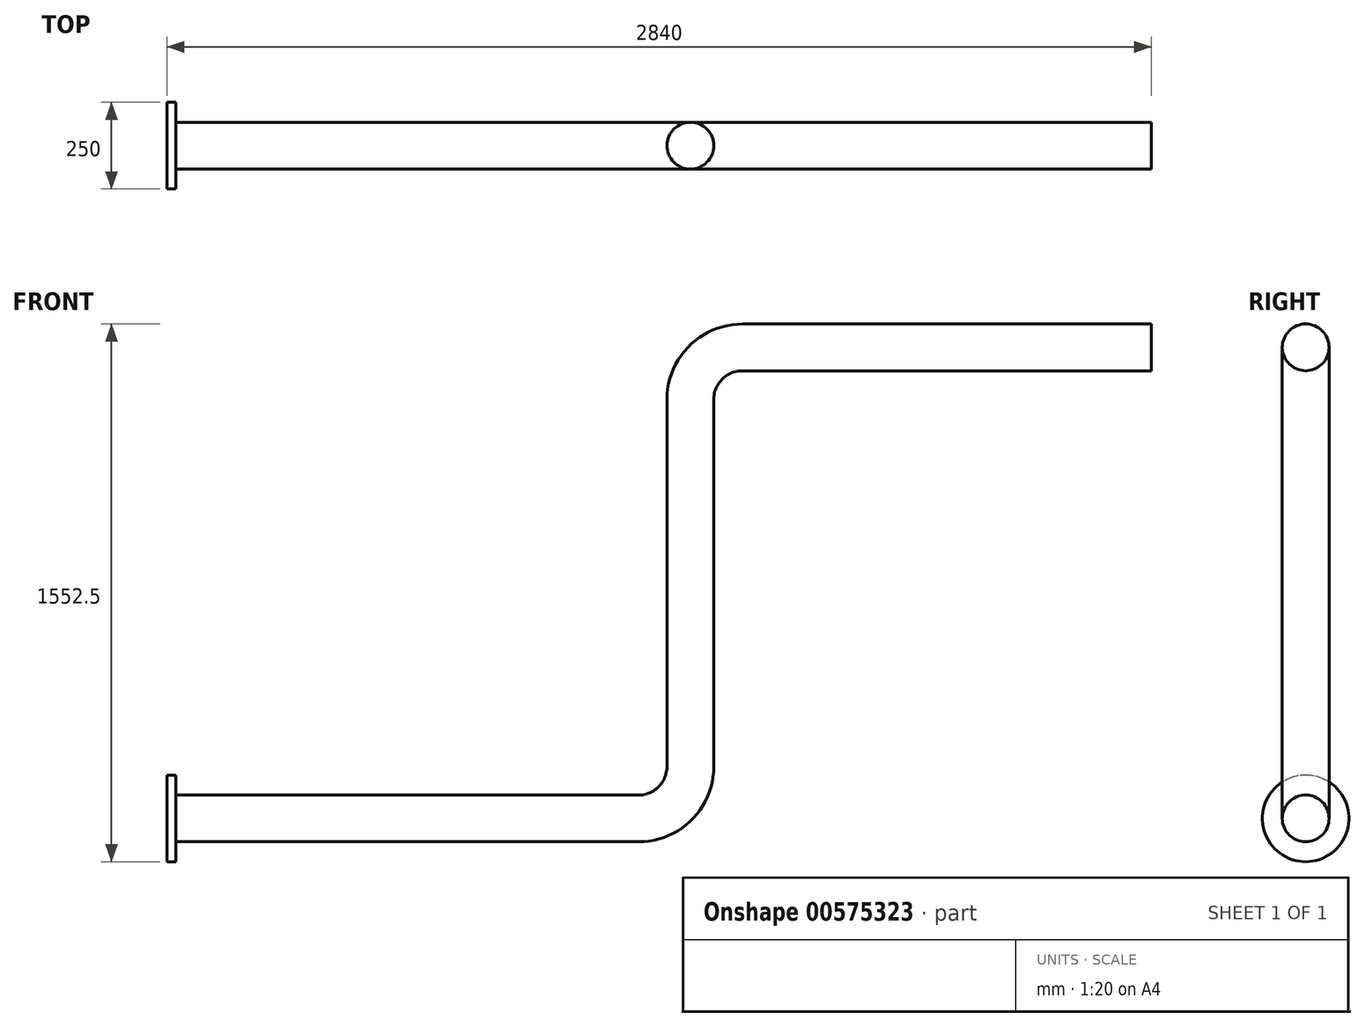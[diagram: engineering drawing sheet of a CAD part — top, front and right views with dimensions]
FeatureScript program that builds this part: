
annotation { "Feature Type Name" : "Feature", "Feature Type Description" : "" }
export const myFeature = defineFeature(function(context is Context, id is Id, definition is map)
    precondition{}
    {
        {
            var Q0;
            Q0=qCreatedBy(makeId("Right.planeOp"),FACE);
            var sketch = newSketch(context, id + "F0", { "sketchPlane" : qUnion([Q0])});
            skCircle(sketch, "E0", {"center": v(0, 0) * mm, "radius": 67.5 * mm});
            skCircle(sketch, "E1", {"center": v(0, 0) * mm, "radius": 125 * mm});
            skSolve(sketch);
        }
        {
            var Q0;
            Q0=qCreatedBy(makeId("Front.planeOp"),FACE);
            var sketch = newSketch(context, id + "F1", { "sketchPlane" : qUnion([Q0])});
            skLineSegment(sketch, "E2", {"start": v(0, 0) * mm, "end": v(1360, 0) * mm});
            skLineSegment(sketch, "E3", {"start": v(1510, 150) * mm, "end": v(1510, 1210) * mm});
            skLineSegment(sketch, "E4", {"start": v(1660, 1360) * mm, "end": v(2840, 1360) * mm});
            skPoint(sketch, "E5.visualSharp", {"position": v(1510, 1360) * mm});
            skArc(sketch, "E5.filletArc", {"start": v(1660, 1360) * mm, "mid": v(1553.93, 1316.07) * mm, "end": v(1510, 1210) * mm});
            skPoint(sketch, "E6.visualSharp", {"position": v(1510, 0) * mm});
            skArc(sketch, "E6.filletArc", {"start": v(1360, 0) * mm, "mid": v(1466.07, 43.93) * mm, "end": v(1510, 150) * mm});
            skSolve(sketch);
        }
        {
            var Q0;
            Q0=makeQuery(id+"F0.imprint","IMPRINT",FACE,{"disambiguationData":[TD([[makeQuery(id+"F0.imprint","IMPRINT",EDGE,{"derivedFrom":sQuery(id+"F0.wireOp",EDGE,"E0")}),1.0]])]});
            var Q1;
            Q1=sQuery(id+"F1.wireOp",EDGE,"E2");
            var Q2;
            Q2=sQuery(id+"F1.wireOp",EDGE,"E6.filletArc");
            var Q3;
            Q3=sQuery(id+"F1.wireOp",EDGE,"E3");
            var Q4;
            Q4=sQuery(id+"F1.wireOp",EDGE,"E5.filletArc");
            var Q5;
            Q5=sQuery(id+"F1.wireOp",EDGE,"E4");
            sweep(context, id + "F2", {"profiles" : qUnion([Q0]), "path" : qUnion([Q1, Q2, Q3, Q4, Q5])});
        }
        {
            var Q0;
            Q0=makeQuery(id+"F0.imprint","IMPRINT",FACE,{"disambiguationData":[TD([[makeQuery(id+"F0.imprint","IMPRINT",EDGE,{"derivedFrom":sQuery(id+"F0.wireOp",EDGE,"E0")}),-1.0]])]});
            extrude(context, id + "F3", {"entities" : qUnion([Q0]), "operationType" : NewBodyOperationType.ADD, "depth" : 25 * mm, "offsetDistance" : 25 * mm});
        }
    });
